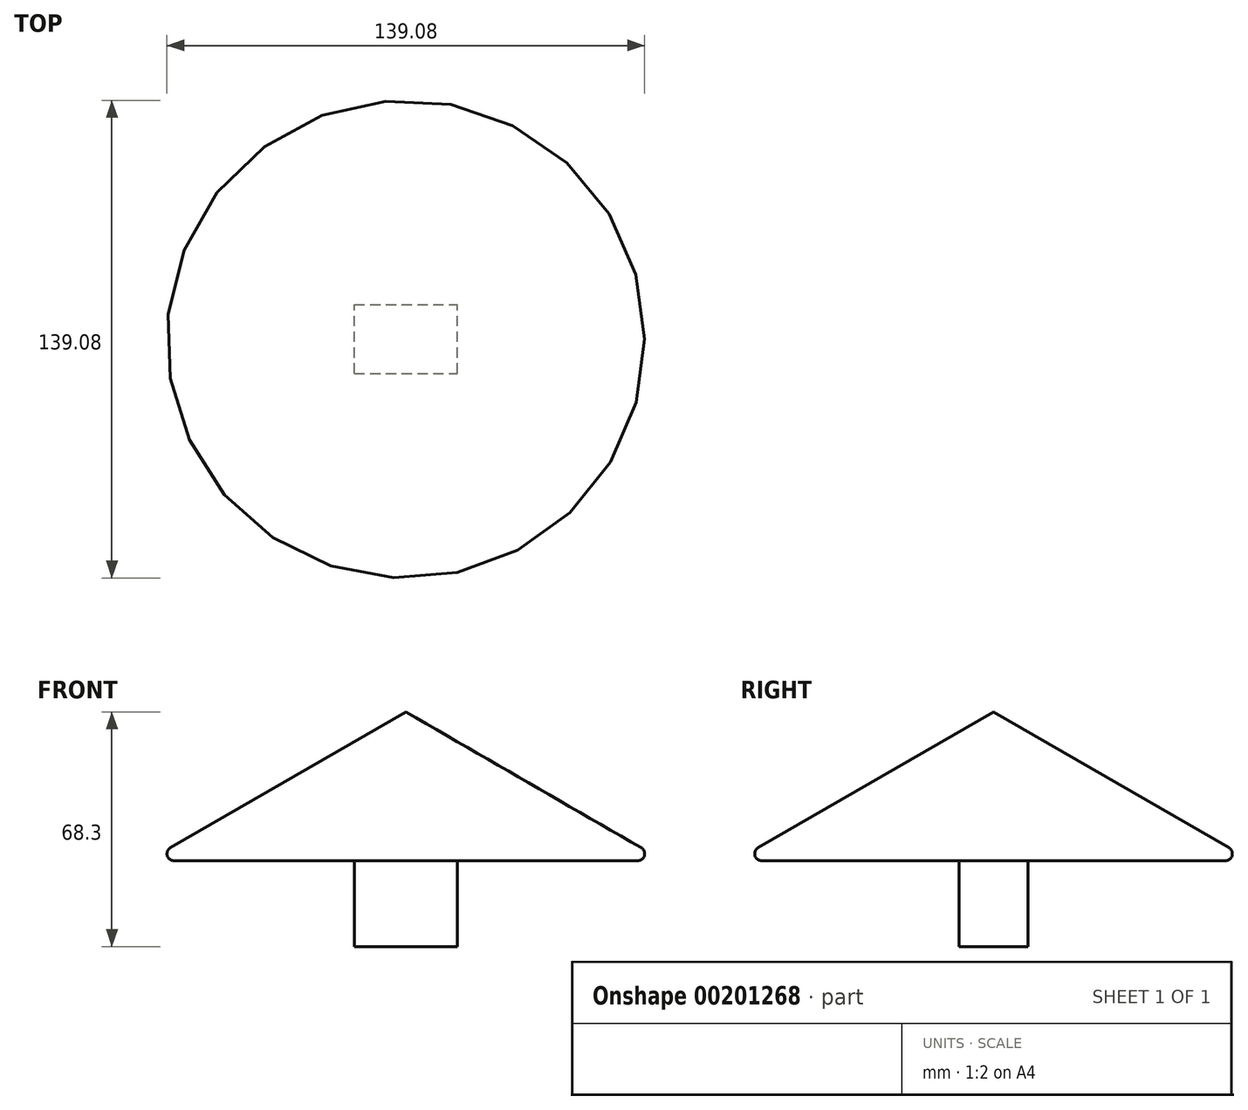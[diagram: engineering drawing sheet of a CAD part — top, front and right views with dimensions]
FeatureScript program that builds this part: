
annotation { "Feature Type Name" : "Feature", "Feature Type Description" : "" }
export const myFeature = defineFeature(function(context is Context, id is Id, definition is map)
    precondition{}
    {
        {
            var Q0;
            Q0=qCreatedBy(makeId("Top.planeOp"),FACE);
            var sketch = newSketch(context, id + "F0", { "sketchPlane" : qUnion([Q0])});
            skCircle(sketch, "E0", {"center": v(0, 0) * mm, "radius": 75 * mm});
            skSolve(sketch);
        }
        {
            var Q0;
            Q0=makeQuery(id+"F0.imprint","IMPRINT",FACE,{"disambiguationData":[TD([[makeQuery(id+"F0.imprint","IMPRINT",EDGE,{"derivedFrom":sQuery(id+"F0.wireOp",EDGE,"E0")}),1.0]])]});
            extrude(context, id + "F1", {"entities" : qUnion([Q0]), "depth" : 50 * mm, "hasDraft" : true, "draftAngle" : 60 * degree, "draftPullDirection" : true});
        }
        {
            var Q0;
            Q0=qCreatedBy(makeId("Top.planeOp"),FACE);
            var sketch = newSketch(context, id + "F2", { "sketchPlane" : qUnion([Q0])});
            skLineSegment(sketch, "E1.bottom", {"start": v(-15, -10) * mm, "end": v(15, -10) * mm});
            skLineSegment(sketch, "E1.top", {"start": v(-15, 10) * mm, "end": v(15, 10) * mm});
            skLineSegment(sketch, "E1.left", {"start": v(-15, -10) * mm, "end": v(-15, 10) * mm});
            skLineSegment(sketch, "E1.right", {"start": v(15, -10) * mm, "end": v(15, 10) * mm});
            skPoint(sketch, "E1.middle", {"position": v(0, 0) * mm});
            skSolve(sketch);
        }
        {
            var Q0;
            Q0=makeQuery(id+"F2.imprint","IMPRINT",FACE,{"disambiguationData":[TD([[makeQuery(id+"F2.imprint","IMPRINT",EDGE,{"derivedFrom":sQuery(id+"F2.wireOp",EDGE,"E1.bottom")}),1.0]])]});
            extrude(context, id + "F3", {"entities" : qUnion([Q0]), "operationType" : NewBodyOperationType.ADD, "oppositeDirection" : true, "depth" : 25 * mm});
        }
        {
            var Q0;
            Q0=makeQuery(id+"F1.opExtrude","CAP_EDGE",EDGE,{"disambiguationData":[OSD([sQuery(id+"F0.wireOp",EDGE,"E0")])],"isStart":true});
            fillet(context, id + "F4", {"entities" : qUnion([Q0]), "radius" : 2 * mm, "tangentPropagation" : true, "allowEdgeOverflow" : false});
        }
    });
